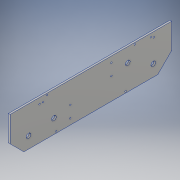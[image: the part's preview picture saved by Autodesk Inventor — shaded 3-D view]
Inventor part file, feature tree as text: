
AUTODESK INVENTOR PART (.ipt)
format: ipt  version: 2017 (Build 210142000, 142)  size: 200,704 bytes
history: native  units: in
note: dims shown in document units (in); Inventor stores cm internally (conversion verified against a paired STEP export)
features: sketch x5, projected_geometry x4, hole x3, extrude x2, chamfer x2
ambient origin geometry x8: Origin, YZ Plane, XZ Plane, XY Plane, X Axis, Y Axis, Z Axis, Center Point
bodies: Solid1 (feature_tree)
feature tree (16):
  extrude  "Extrusion1"  Depth=17.5in
  chamfer  "Chamfer1"  Distance=0.1875in
  chamfer  "Chamfer2"  Distance=1.5in Angle=45.0deg
  extrude  "Extrusion2"  Depth=0.1875in TaperAngle=45.0deg
  hole  "Hole1"  [1 undecoded]
  hole  "Hole2"  [1 undecoded]
  hole  "Hole3"  [1 undecoded]
  sketch  "Sketch1"  dims[d0=4.25in d1=17.5in]
  sketch  "Sketch2"  dims[d2=0.501in]
  projected_geometry  "Projected Loop1"
  sketch  "Sketch6"  dims[d3=1.25in]
  projected_geometry  "Projected Loop5"
  sketch  "Sketch7"  dims[d4=2.0in]
  projected_geometry  "Projected Loop6"
  sketch  "Sketch8"  dims[d5=2.0in d6=0.1875in d7=0.0in d8=1.5in d9=0.125in d10=45.0deg d11=1.5in d12=0.125in d13=45.0deg d14=0.501in d15=4.75in d17=0.501in d19=4.75in d20=1.0in d21=0.0in d22=6.517in d23=0.125in d24=0.603in d25=0.125in d26=0.63in d27=6.517in d28=0.125in d29=0.603in d30=6.517in d31=0.125in d32=0.63in d33=6.517in d78=1.535in d79=1.535in d80=1.776in d81=1.776in d82=1.26in d83=0.63in d84=1.26in d85=0.63in d86=1.776in d87=1.776in d88=0.15in d89=0.75in d90=0.375in d91=0.25in d92=0.5635in d93=1.0in d94=0.8108in d95=0.625in d96=0.625in d97=0.375in d98=3.1875in d99=0.375in d100=2.25in d101=0.1924in d102=0.75in d103=0.15in d104=0.75in d105=0.375in d106=0.25in d107=0.5635in d108=1.0in d109=0.8108in d110=0.175in d111=0.175in d112=4.0in d113=4.0in d114=0.175in d115=0.175in d116=0.15in d117=0.75in d118=0.375in d119=0.25in d120=0.5635in d121=1.0in d122=0.8108in d123=5.0in d124=5.0in]
  projected_geometry  "Projected Loop7"
note: 3 required parameter values undecoded (feature->parameter linkage not recoverable at this tier; creation-order binding heuristic only, values carry confidence <= 0.55)
